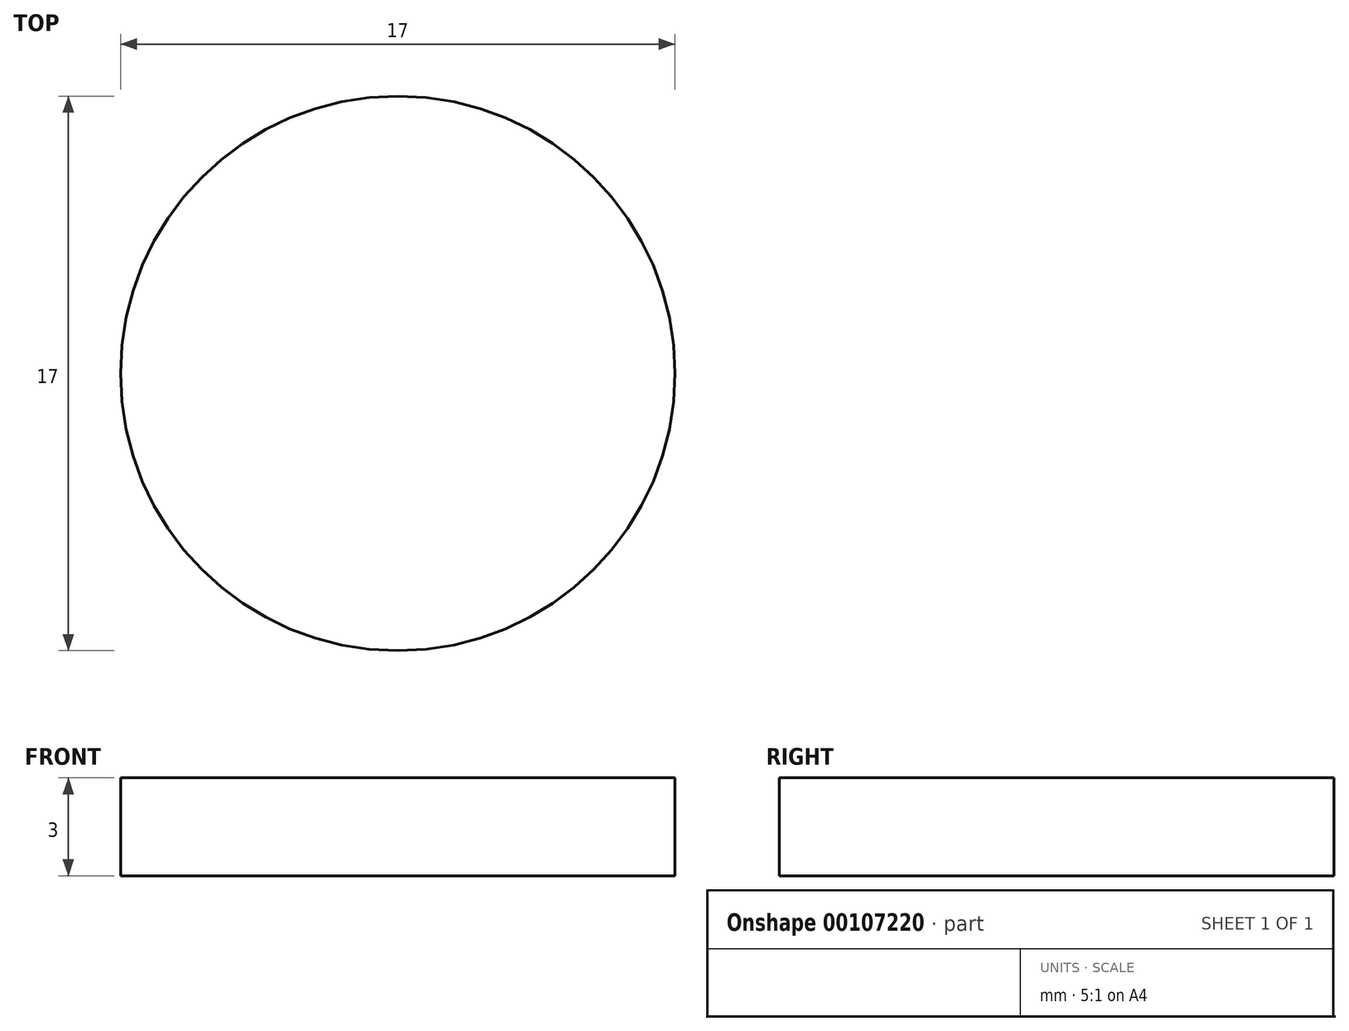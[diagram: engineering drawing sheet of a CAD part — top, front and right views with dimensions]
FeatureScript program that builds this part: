
annotation { "Feature Type Name" : "Feature", "Feature Type Description" : "" }
export const myFeature = defineFeature(function(context is Context, id is Id, definition is map)
    precondition{}
    {
        {
            var Q0;
            Q0=qCreatedBy(makeId("Top.planeOp"),FACE);
            var sketch = newSketch(context, id + "F0", { "sketchPlane" : qUnion([Q0])});
            skCircle(sketch, "E0", {"center": v(0, 0) * mm, "radius": 8.5 * mm});
            skSolve(sketch);
        }
        {
            var Q0;
            Q0=makeQuery(id+"F0.imprint","IMPRINT",FACE,{"disambiguationData":[TD([[makeQuery(id+"F0.imprint","IMPRINT",EDGE,{"derivedFrom":sQuery(id+"F0.wireOp",EDGE,"E0")}),1.0]])]});
            extrude(context, id + "F1", {"entities" : qUnion([Q0]), "depth" : 3 * mm});
        }
    });
